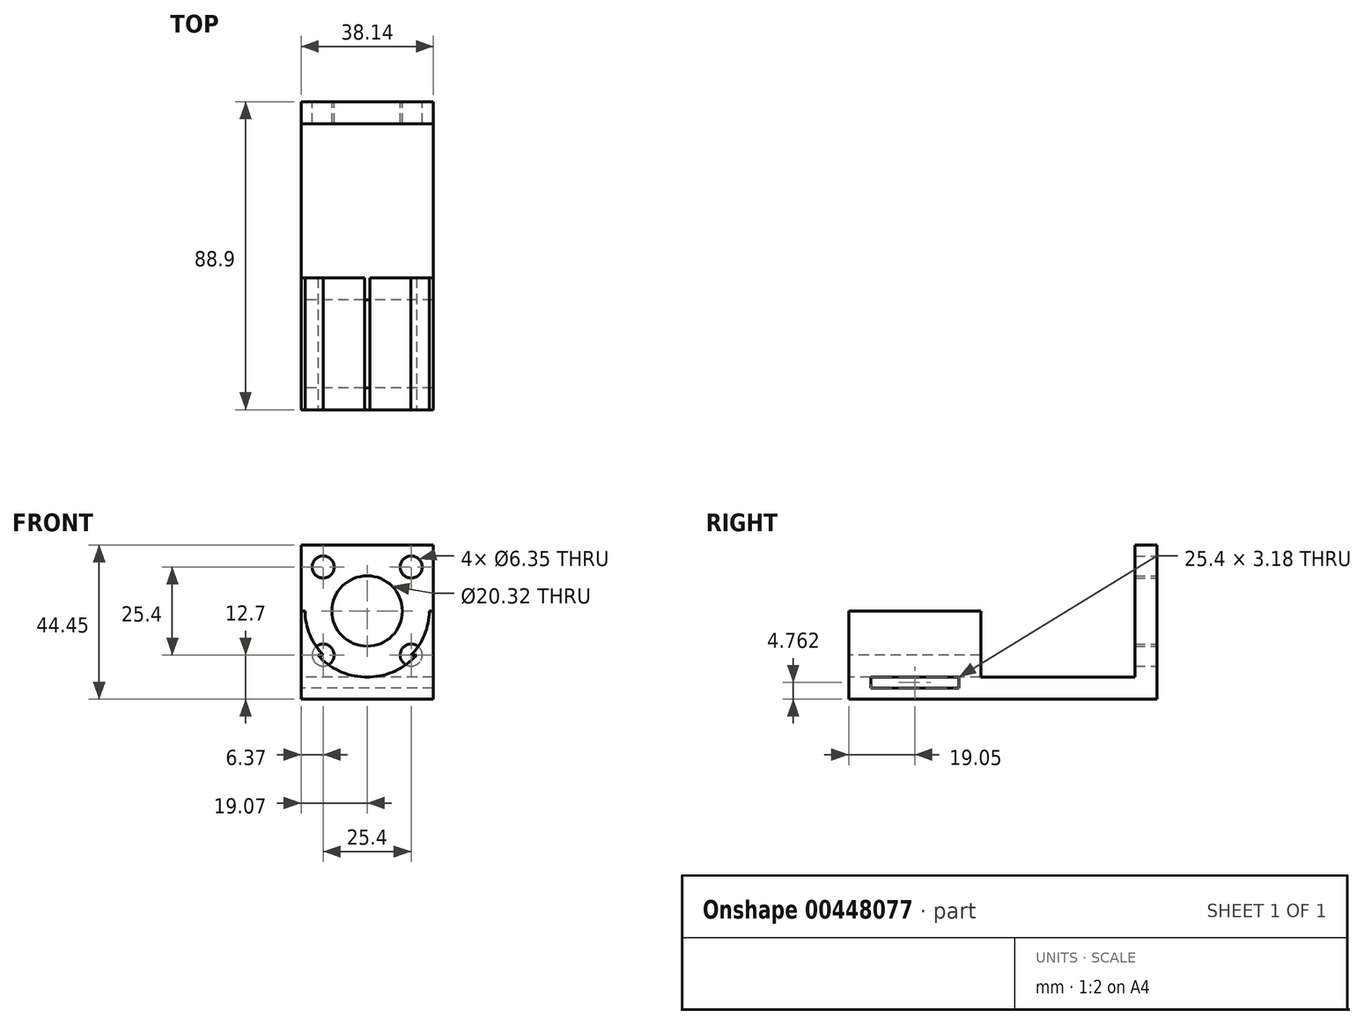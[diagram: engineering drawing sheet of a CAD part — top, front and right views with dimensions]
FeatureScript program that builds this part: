
annotation { "Feature Type Name" : "Feature", "Feature Type Description" : "" }
export const myFeature = defineFeature(function(context is Context, id is Id, definition is map)
    precondition{}
    {
        {
            var Q0;
            Q0=qCreatedBy(makeId("Front.planeOp"),FACE);
            var sketch = newSketch(context, id + "F0", { "sketchPlane" : qUnion([Q0])});
            skLineSegment(sketch, "E0.bottom", {"start": v(-19.05, 19.05) * mm, "end": v(19.05, 19.05) * mm});
            skLineSegment(sketch, "E0.top", {"start": v(-19.05, -19.05) * mm, "end": v(19.05, -19.05) * mm});
            skLineSegment(sketch, "E0.left", {"start": v(-19.05, 19.05) * mm, "end": v(-19.05, -19.05) * mm});
            skLineSegment(sketch, "E0.right", {"start": v(19.05, 19.05) * mm, "end": v(19.05, -19.05) * mm});
            skPoint(sketch, "E0.middle", {"position": v(0, 0) * mm});
            skCircle(sketch, "E1", {"center": v(0, 0) * mm, "radius": 10.16 * mm});
            skCircle(sketch, "E2", {"center": v(-12.7, 12.7) * mm, "radius": 3.18 * mm});
            skCircle(sketch, "E3.MirrorC", {"center": v(12.7, 12.7) * mm, "radius": 3.18 * mm});
            skCircle(sketch, "E4.MirrorC", {"center": v(-12.7, -12.7) * mm, "radius": 3.18 * mm});
            skCircle(sketch, "E5.MirrorC", {"center": v(12.7, -12.7) * mm, "radius": 3.18 * mm});
            skSolve(sketch);
        }
        {
            var Q0;
            Q0 = qSketchRegion(id + "F0", true);
            extrude(context, id + "F1", {"entities" : qUnion([Q0]), "depth" : 6.35 * mm});
        }
        {
            var Q0;
            Q0=makeQuery(id+"F1.opExtrude","SWEPT_FACE",FACE,{"disambiguationData":[OSD([sQuery(id+"F0.wireOp",EDGE,"E0.top")])]});
            var sketch = newSketch(context, id + "F2", { "sketchPlane" : qUnion([Q0])});
            skLineSegment(sketch, "E6.bottom", {"start": v(-19.05, 0) * mm, "end": v(19.05, 0) * mm});
            skLineSegment(sketch, "E6.top", {"start": v(-19.05, 88.9) * mm, "end": v(19.05, 88.9) * mm});
            skLineSegment(sketch, "E6.left", {"start": v(-19.05, 0) * mm, "end": v(-19.05, 88.9) * mm});
            skLineSegment(sketch, "E6.right", {"start": v(19.05, 0) * mm, "end": v(19.05, 88.9) * mm});
            skSolve(sketch);
        }
        {
            var Q0;
            Q0 = qSketchRegion(id + "F2", true);
            extrude(context, id + "F3", {"entities" : qUnion([Q0]), "operationType" : NewBodyOperationType.ADD, "depth" : 6.35 * mm});
        }
        {
            var Q0;
            Q0=makeQuery(id+"F3.opExtrude","SWEPT_FACE",FACE,{"disambiguationData":[OSD([sQuery(id+"F2.wireOp",EDGE,"E6.top")])]});
            var sketch = newSketch(context, id + "F4", { "sketchPlane" : qUnion([Q0])});
            skLineSegment(sketch, "E7.bottom", {"start": v(-19.05, -19.05) * mm, "end": v(19.05, -19.05) * mm});
            skLineSegment(sketch, "E7.top", {"start": v(-19.05, -12.7) * mm, "end": v(19.05, -12.7) * mm});
            skLineSegment(sketch, "E7.left", {"start": v(-19.05, -19.05) * mm, "end": v(-19.05, -12.7) * mm});
            skLineSegment(sketch, "E7.right", {"start": v(19.05, -19.05) * mm, "end": v(19.05, -12.7) * mm});
            skLineSegment(sketch, "E8", {"start": v(0, -12.7) * mm, "end": v(0, 0) * mm});
            skArc(sketch, "E9", {"start": v(0, -17.9) * mm, "mid": v(12.66, -12.66) * mm, "end": v(17.9, 0) * mm});
            skPoint(sketch, "E9.startSnap0", {"position": v(0, -19.05) * mm});
            skArc(sketch, "E10.MirrorCS", {"start": v(0, -17.9) * mm, "mid": v(-12.66, -12.66) * mm, "end": v(-17.9, 0) * mm});
            skArc(sketch, "E11", {"start": v(-19.07, 0) * mm, "mid": v(0, -19.07) * mm, "end": v(19.07, 0) * mm});
            skLineSegment(sketch, "E12", {"start": v(-17.9, 0) * mm, "end": v(-19.07, 0) * mm});
            skLineSegment(sketch, "E13", {"start": v(17.9, 0) * mm, "end": v(19.07, 0) * mm});
            skLineSegment(sketch, "E14", {"start": v(-19.07, 0) * mm, "end": v(-19.05, -12.7) * mm});
            skLineSegment(sketch, "E15", {"start": v(19.07, 0) * mm, "end": v(19.05, -12.7) * mm});
            skSolve(sketch);
        }
        {
            var Q0;
            {var subQ5=sQuery(id+"F4.wireOp",EDGE,"E12");Q0=makeQuery(id+"F4.imprint","IMPRINT",FACE,{"disambiguationData":[TD([[makeQuery(id+"F4.imprint","IMPRINT",EDGE,{"derivedFrom":subQ5}),1.0]])]});}
            var Q1;
            {var subQ5=sQuery(id+"F4.wireOp",EDGE,"E13");Q1=makeQuery(id+"F4.imprint","IMPRINT",FACE,{"disambiguationData":[TD([[makeQuery(id+"F4.imprint","IMPRINT",EDGE,{"derivedFrom":subQ5}),-1.0]])]});}
            var Q2;
            {var subQ0=sQuery(id+"F4.wireOp",EDGE,"E7.left");Q2=makeQuery(id+"F4.imprint","IMPRINT",FACE,{"disambiguationData":[TD([[makeQuery(id+"F4.imprint","IMPRINT",EDGE,{"derivedFrom":subQ0}),-1.0]])]});}
            var Q3;
            {var subQ0=sQuery(id+"F4.wireOp",EDGE,"E11");var subQ1=sQuery(id+"F4.wireOp",EDGE,"E7.bottom");var subQ2=makeQuery(id+"F4.imprint","INTERSECT",VERTEX,{"disambiguationData":[OD(0.0)],"derivedFrom":[subQ1,subQ0]});Q3=makeQuery(id+"F4.imprint","IMPRINT",FACE,{"disambiguationData":[TD([[makeQuery(id+"F4.imprint","IMPRINT",EDGE,{"disambiguationData":[TD([[subQ2,-1.0]])],"derivedFrom":subQ1}),-1.0]])]});}
            var Q4;
            {var subQ0=sQuery(id+"F4.wireOp",EDGE,"E7.right");Q4=makeQuery(id+"F4.imprint","IMPRINT",FACE,{"disambiguationData":[TD([[makeQuery(id+"F4.imprint","IMPRINT",EDGE,{"derivedFrom":subQ0}),1.0]])]});}
            var Q5;
            {var subQ3=sQuery(id+"F4.wireOp",EDGE,"E11");var subQ5=sQuery(id+"F4.wireOp",EDGE,"E7.bottom");var subQ11=makeQuery(id+"F4.imprint","INTERSECT",VERTEX,{"disambiguationData":[OD(0.0)],"derivedFrom":[subQ5,subQ3]});Q5=makeQuery(id+"F4.imprint","IMPRINT",FACE,{"disambiguationData":[TD([[makeQuery(id+"F4.imprint","IMPRINT",EDGE,{"disambiguationData":[TD([[subQ11,-1.0]])],"derivedFrom":subQ5}),1.0]])]});}
            var Q6;
            {var subQ0=sQuery(id+"F4.wireOp",EDGE,"E14");var subQ3=sQuery(id+"F4.wireOp",EDGE,"E11");var subQ5=makeQuery(id+"F4.imprint","INTERSECT",VERTEX,{"derivedFrom":[subQ3,subQ0]});Q6=makeQuery(id+"F4.imprint","IMPRINT",FACE,{"disambiguationData":[TD([[makeQuery(id+"F4.imprint","IMPRINT",EDGE,{"disambiguationData":[TD([[subQ5,-1.0]])],"derivedFrom":subQ3}),-1.0]])]});}
            var Q7;
            {var subQ0=sQuery(id+"F4.wireOp",EDGE,"E15");var subQ3=sQuery(id+"F4.wireOp",EDGE,"E11");var subQ5=makeQuery(id+"F4.imprint","INTERSECT",VERTEX,{"derivedFrom":[subQ3,subQ0]});Q7=makeQuery(id+"F4.imprint","IMPRINT",FACE,{"disambiguationData":[TD([[makeQuery(id+"F4.imprint","IMPRINT",EDGE,{"disambiguationData":[TD([[subQ5,1.0]])],"derivedFrom":subQ3}),-1.0]])]});}
            extrude(context, id + "F5", {"entities" : qUnion([Q0, Q1, Q2, Q3, Q4, Q5, Q6, Q7]), "operationType" : NewBodyOperationType.ADD, "oppositeDirection" : true, "depth" : 38.1 * mm});
        }
        {
            var Q0;
            Q0=makeQuery(id+"F5.boolean.opBoolean","MERGE",FACE,{"derivedFrom":[makeQuery(id+"F3.boolean.opBoolean","MERGE",FACE,{"derivedFrom":[makeQuery(id+"F1.opExtrude","SWEPT_FACE",FACE,{"disambiguationData":[OSD([sQuery(id+"F0.wireOp",EDGE,"E0.left")])]}),makeQuery(id+"F3.opExtrude","SWEPT_FACE",FACE,{"disambiguationData":[OSD([sQuery(id+"F2.wireOp",EDGE,"E6.left")])]})]}),makeQuery(id+"F5.opExtrude","SWEPT_FACE",FACE,{"disambiguationData":[OSD([sQuery(id+"F4.wireOp",EDGE,"E7.left")])]})]});
            var sketch = newSketch(context, id + "F6", { "sketchPlane" : qUnion([Q0])});
            skLineSegment(sketch, "E16.bottom", {"start": v(50.8, -19.05) * mm, "end": v(88.9, -19.05) * mm});
            skLineSegment(sketch, "E16.top", {"start": v(50.8, -12.7) * mm, "end": v(88.9, -12.7) * mm});
            skLineSegment(sketch, "E16.left", {"start": v(50.8, -19.05) * mm, "end": v(50.8, -12.7) * mm});
            skLineSegment(sketch, "E16.right", {"start": v(88.9, -19.05) * mm, "end": v(88.9, -12.7) * mm});
            skLineSegment(sketch, "E17.top", {"start": v(50.8, -25.4) * mm, "end": v(88.9, -25.4) * mm});
            skLineSegment(sketch, "E17.left", {"start": v(50.8, -19.05) * mm, "end": v(50.8, -25.4) * mm});
            skLineSegment(sketch, "E17.right", {"start": v(88.9, -19.05) * mm, "end": v(88.9, -25.4) * mm});
            skLineSegment(sketch, "E18.top", {"start": v(50.8, -22.23) * mm, "end": v(88.9, -22.23) * mm});
            skLineSegment(sketch, "E18.left", {"start": v(50.8, -19.05) * mm, "end": v(50.8, -22.23) * mm});
            skLineSegment(sketch, "E18.right", {"start": v(88.9, -19.05) * mm, "end": v(88.9, -22.23) * mm});
            skLineSegment(sketch, "E19.top", {"start": v(50.8, -15.88) * mm, "end": v(88.9, -15.88) * mm});
            skLineSegment(sketch, "E19.left", {"start": v(50.8, -19.05) * mm, "end": v(50.8, -15.88) * mm});
            skLineSegment(sketch, "E19.right", {"start": v(88.9, -19.05) * mm, "end": v(88.9, -15.88) * mm});
            skLineSegment(sketch, "E20", {"start": v(82.55, -19.05) * mm, "end": v(82.55, -22.23) * mm});
            skLineSegment(sketch, "E21", {"start": v(57.15, -19.05) * mm, "end": v(57.15, -22.23) * mm});
            skSolve(sketch);
        }
        {
            var Q0;
            {var subQ0=sQuery(id+"F6.wireOp",EDGE,"E20");Q0=makeQuery(id+"F6.imprint","IMPRINT",FACE,{"disambiguationData":[TD([[makeQuery(id+"F6.imprint","IMPRINT",EDGE,{"derivedFrom":subQ0}),-1.0]])]});}
            extrude(context, id + "F7", {"entities" : qUnion([Q0]), "operationType" : NewBodyOperationType.REMOVE, "endBound" : BoundingType.THROUGH_ALL, "oppositeDirection" : true, "depth" : 25.4 * mm});
        }
    });
